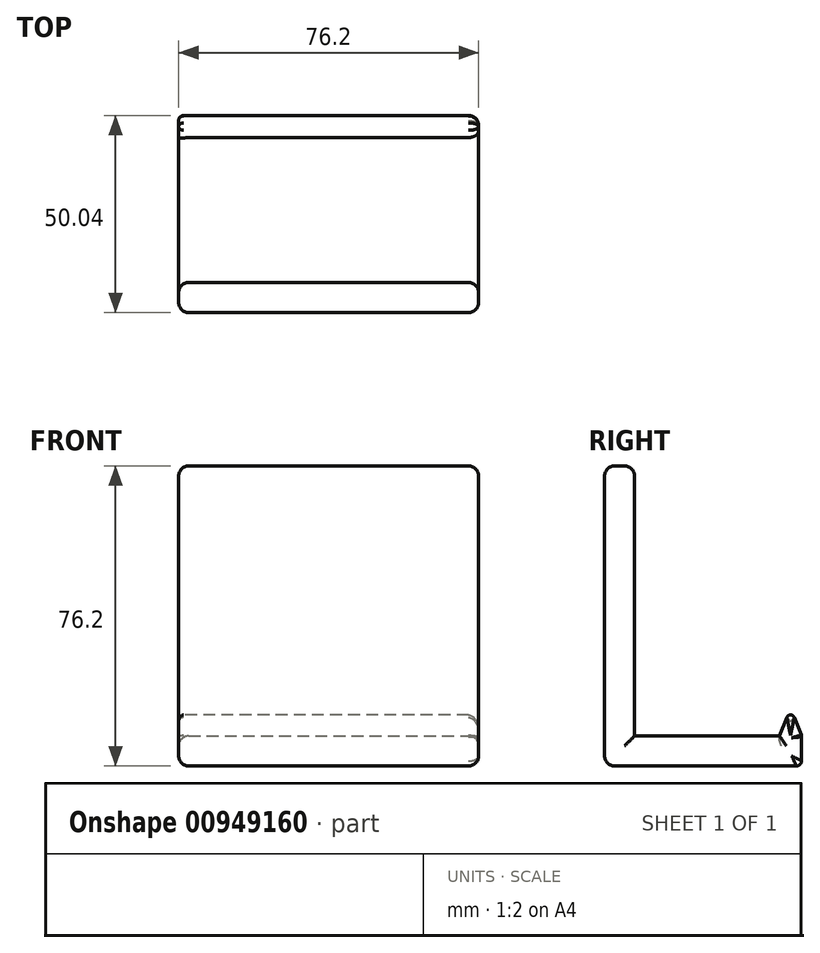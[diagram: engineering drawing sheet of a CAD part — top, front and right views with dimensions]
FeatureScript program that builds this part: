
annotation { "Feature Type Name" : "Feature", "Feature Type Description" : "" }
export const myFeature = defineFeature(function(context is Context, id is Id, definition is map)
    precondition{}
    {
        {
            var Q0;
            Q0=qCreatedBy(makeId("Front.planeOp"),FACE);
            var sketch = newSketch(context, id + "F0", { "sketchPlane" : qUnion([Q0])});
            skLineSegment(sketch, "E0", {"start": v(-13.67, 0) * mm, "end": v(62.53, 0) * mm});
            skLineSegment(sketch, "E1", {"start": v(-13.67, 0) * mm, "end": v(-13.67, 7.62) * mm});
            skLineSegment(sketch, "E2", {"start": v(62.53, 0) * mm, "end": v(62.53, 7.62) * mm});
            skLineSegment(sketch, "E3", {"start": v(-13.67, 7.62) * mm, "end": v(62.53, 7.62) * mm});
            skLineSegment(sketch, "E4", {"start": v(-141.5, -14.66) * mm, "end": v(-139.83, -11.9) * mm});
            skSolve(sketch);
        }
        {
            var Q0;
            Q0=makeQuery(id+"F0.imprint","IMPRINT",FACE,{"disambiguationData":[TD([[makeQuery(id+"F0.imprint","IMPRINT",EDGE,{"derivedFrom":sQuery(id+"F0.wireOp",EDGE,"E0")}),1.0]])]});
            extrude(context, id + "F1", {"entities" : qUnion([Q0]), "depth" : 50.04 * mm, "offsetDistance" : 25.4 * mm});
        }
        {
            var Q0;
            Q0=makeQuery(id+"F1.opExtrude","SWEPT_FACE",FACE,{"disambiguationData":[OSD([sQuery(id+"F0.wireOp",EDGE,"E3")])]});
            var sketch = newSketch(context, id + "F2", { "sketchPlane" : qUnion([Q0])});
            skLineSegment(sketch, "E5.bottom", {"start": v(-13.67, -50.04) * mm, "end": v(62.53, -50.04) * mm});
            skLineSegment(sketch, "E5.top", {"start": v(-13.67, -42.42) * mm, "end": v(62.53, -42.42) * mm});
            skLineSegment(sketch, "E5.left", {"start": v(-13.67, -50.04) * mm, "end": v(-13.67, -42.42) * mm});
            skLineSegment(sketch, "E5.right", {"start": v(62.53, -50.04) * mm, "end": v(62.53, -42.42) * mm});
            skSolve(sketch);
        }
        {
            var Q0;
            Q0=makeQuery(id+"F2.imprint","IMPRINT",FACE,{"disambiguationData":[TD([[makeQuery(id+"F2.imprint","IMPRINT",EDGE,{"derivedFrom":sQuery(id+"F2.wireOp",EDGE,"E5.bottom")}),1.0]])]});
            extrude(context, id + "F3", {"entities" : qUnion([Q0]), "operationType" : NewBodyOperationType.ADD, "depth" : 68.58 * mm, "offsetDistance" : 25.4 * mm});
        }
        {
            var Q0;
            Q0=makeQuery(id+"F3.boolean.opBoolean","MERGE",FACE,{"derivedFrom":[makeQuery(id+"F1.opExtrude","SWEPT_FACE",FACE,{"disambiguationData":[OSD([sQuery(id+"F0.wireOp",EDGE,"E1")])]}),makeQuery(id+"F3.opExtrude","SWEPT_FACE",FACE,{"disambiguationData":[OSD([sQuery(id+"F2.wireOp",EDGE,"E5.left")])]})]});
            var sketch = newSketch(context, id + "F4", { "sketchPlane" : qUnion([Q0])});
            skLineSegment(sketch, "E6", {"start": v(0, 7.62) * mm, "end": v(5.59, 7.62) * mm});
            skLineSegment(sketch, "E7", {"start": v(5.59, 7.62) * mm, "end": v(2.8, 14.7) * mm});
            skLineSegment(sketch, "E8", {"start": v(2.8, 14.7) * mm, "end": v(0, 7.62) * mm});
            skSolve(sketch);
        }
        {
            var Q0;
            Q0=makeQuery(id+"F4.imprint","IMPRINT",FACE,{"disambiguationData":[TD([[makeQuery(id+"F4.imprint","IMPRINT",EDGE,{"derivedFrom":sQuery(id+"F4.wireOp",EDGE,"E6")}),-1.0]])]});
            extrude(context, id + "F5", {"entities" : qUnion([Q0]), "operationType" : NewBodyOperationType.ADD, "oppositeDirection" : true, "depth" : 76.2 * mm, "offsetDistance" : 25.4 * mm});
        }
        {
            var Q0;
            Q0=makeQuery(id+"F5.opExtrude","SWEPT_EDGE",EDGE,{"disambiguationData":[OSD([sQuery(id+"F4.wireOp",EDGE,"E7"),sQuery(id+"F4.wireOp",EDGE,"E8")])]});
            fillet(context, id + "F6", {"entities" : qUnion([Q0]), "radius" : 1.02 * mm, "tangentPropagation" : true, "allowEdgeOverflow" : false});
        }
        {
            var Q0;
            Q0=makeQuery(id+"F3.opExtrude","CAP_EDGE",EDGE,{"disambiguationData":[OSD([sQuery(id+"F2.wireOp",EDGE,"E5.top")])],"isStart":false});
            fillet(context, id + "F7", {"entities" : qUnion([Q0]), "radius" : 2.54 * mm, "tangentPropagation" : true, "allowEdgeOverflow" : false});
        }
        {
            var Q0;
            Q0=makeQuery(id+"F3.opExtrude","CAP_EDGE",EDGE,{"disambiguationData":[OSD([sQuery(id+"F2.wireOp",EDGE,"E5.bottom")])],"isStart":false});
            fillet(context, id + "F8", {"entities" : qUnion([Q0]), "radius" : 2.54 * mm, "tangentPropagation" : true, "allowEdgeOverflow" : false});
        }
        {
            var Q0;
            Q0=makeQuery(id+"F3.boolean.opBoolean","MERGE",EDGE,{"derivedFrom":[makeQuery(id+"F1.opExtrude","CAP_EDGE",EDGE,{"disambiguationData":[OSD([sQuery(id+"F0.wireOp",EDGE,"E1")])],"isStart":false}),makeQuery(id+"F3.opExtrude","SWEPT_EDGE",EDGE,{"disambiguationData":[OSD([sQuery(id+"F2.wireOp",EDGE,"E5.bottom"),sQuery(id+"F2.wireOp",EDGE,"E5.left")])]})]});
            var Q1;
            Q1=makeQuery(id+"F3.opExtrude","SWEPT_EDGE",EDGE,{"disambiguationData":[OSD([sQuery(id+"F0.wireOp",EDGE,"E1"),sQuery(id+"F0.wireOp",EDGE,"E3"),sQuery(id+"F2.wireOp",EDGE,"E5.top"),sQuery(id+"F2.wireOp",EDGE,"E5.left")])]});
            var Q2;
            Q2=makeQuery(id+"F1.opExtrude","SWEPT_EDGE",EDGE,{"disambiguationData":[OSD([sQuery(id+"F0.wireOp",EDGE,"E0"),sQuery(id+"F0.wireOp",EDGE,"E1")])]});
            fillet(context, id + "F9", {"entities" : qUnion([Q0, Q1, Q2]), "radius" : 2.54 * mm, "tangentPropagation" : true, "allowEdgeOverflow" : false});
        }
        {
            var Q0;
            Q0=makeQuery(id+"F1.opExtrude","SWEPT_EDGE",EDGE,{"disambiguationData":[OSD([sQuery(id+"F0.wireOp",EDGE,"E1"),sQuery(id+"F0.wireOp",EDGE,"E3")])]});
            fillet(context, id + "F10", {"entities" : qUnion([Q0]), "radius" : 2.54 * mm, "tangentPropagation" : true, "allowEdgeOverflow" : false});
        }
        {
            var Q0;
            Q0=makeQuery(id+"F5.opExtrude","CAP_EDGE",EDGE,{"disambiguationData":[OSD([sQuery(id+"F4.wireOp",EDGE,"E7")])],"isStart":true});
            fillet(context, id + "F11", {"entities" : qUnion([Q0]), "radius" : 1.27 * mm, "tangentPropagation" : true, "allowEdgeOverflow" : false});
        }
        {
            var Q0;
            Q0=makeQuery(id+"F11.opFillet","BLEND_EDGE",EDGE,{"blendedFrom":[makeQuery(id+"F5.opExtrude","CAP_EDGE",EDGE,{"disambiguationData":[OSD([sQuery(id+"F4.wireOp",EDGE,"E8")])],"isStart":true}),makeQuery(id+"F1.opExtrude","CAP_FACE",FACE,{"disambiguationData":[OSD([sQuery(id+"F0.wireOp",EDGE,"E0"),sQuery(id+"F0.wireOp",EDGE,"E1"),sQuery(id+"F0.wireOp",EDGE,"E2"),sQuery(id+"F0.wireOp",EDGE,"E3")])],"isStart":true})],"blendedInto":[makeQuery(id+"F1.opExtrude","CAP_FACE",FACE,{"disambiguationData":[OSD([sQuery(id+"F0.wireOp",EDGE,"E0"),sQuery(id+"F0.wireOp",EDGE,"E1"),sQuery(id+"F0.wireOp",EDGE,"E2"),sQuery(id+"F0.wireOp",EDGE,"E3")])],"isStart":true})]});
            var Q1;
            Q1=makeQuery(id+"F1.opExtrude","CAP_EDGE",EDGE,{"disambiguationData":[OSD([sQuery(id+"F0.wireOp",EDGE,"E1")])],"isStart":true});
            var Q2;
            {var subQ0=sQuery(id+"F0.wireOp",EDGE,"E1");var subQ1=sQuery(id+"F0.wireOp",EDGE,"E0");Q2=makeQuery(id+"F9.opFillet","BLEND_EDGE",EDGE,{"blendedFrom":[makeQuery(id+"F1.opExtrude","SWEPT_EDGE",EDGE,{"disambiguationData":[OSD([subQ1,subQ0])]}),makeQuery(id+"F1.opExtrude","CAP_FACE",FACE,{"disambiguationData":[OSD([subQ1,subQ0,sQuery(id+"F0.wireOp",EDGE,"E2"),sQuery(id+"F0.wireOp",EDGE,"E3")])],"isStart":true})],"blendedInto":[makeQuery(id+"F1.opExtrude","CAP_FACE",FACE,{"disambiguationData":[OSD([subQ1,subQ0,sQuery(id+"F0.wireOp",EDGE,"E2"),sQuery(id+"F0.wireOp",EDGE,"E3")])],"isStart":true})]});}
            fillet(context, id + "F12", {"entities" : qUnion([Q0, Q1, Q2]), "radius" : 1.27 * mm, "tangentPropagation" : true, "allowEdgeOverflow" : false});
        }
        {
            var Q0;
            Q0=makeQuery(id+"F1.opExtrude","SWEPT_EDGE",EDGE,{"disambiguationData":[OSD([sQuery(id+"F0.wireOp",EDGE,"E0"),sQuery(id+"F0.wireOp",EDGE,"E2")])]});
            fillet(context, id + "F13", {"entities" : qUnion([Q0]), "radius" : 2.54 * mm, "tangentPropagation" : true, "allowEdgeOverflow" : false});
        }
        {
            var Q0;
            Q0=makeQuery(id+"F1.opExtrude","SWEPT_EDGE",EDGE,{"disambiguationData":[OSD([sQuery(id+"F0.wireOp",EDGE,"E2"),sQuery(id+"F0.wireOp",EDGE,"E3")])]});
            fillet(context, id + "F14", {"entities" : qUnion([Q0]), "radius" : 2.54 * mm, "tangentPropagation" : true, "allowEdgeOverflow" : false});
        }
        {
            var Q0;
            Q0=makeQuery(id+"F3.opExtrude","SWEPT_EDGE",EDGE,{"disambiguationData":[OSD([sQuery(id+"F0.wireOp",EDGE,"E2"),sQuery(id+"F0.wireOp",EDGE,"E3"),sQuery(id+"F2.wireOp",EDGE,"E5.top"),sQuery(id+"F2.wireOp",EDGE,"E5.right")])]});
            var Q1;
            Q1=makeQuery(id+"F3.boolean.opBoolean","MERGE",EDGE,{"derivedFrom":[makeQuery(id+"F1.opExtrude","CAP_EDGE",EDGE,{"disambiguationData":[OSD([sQuery(id+"F0.wireOp",EDGE,"E2")])],"isStart":false}),makeQuery(id+"F3.opExtrude","SWEPT_EDGE",EDGE,{"disambiguationData":[OSD([sQuery(id+"F2.wireOp",EDGE,"E5.bottom"),sQuery(id+"F2.wireOp",EDGE,"E5.right")])]})]});
            fillet(context, id + "F15", {"entities" : qUnion([Q0, Q1]), "radius" : 2.54 * mm, "tangentPropagation" : true, "allowEdgeOverflow" : false});
        }
    });
